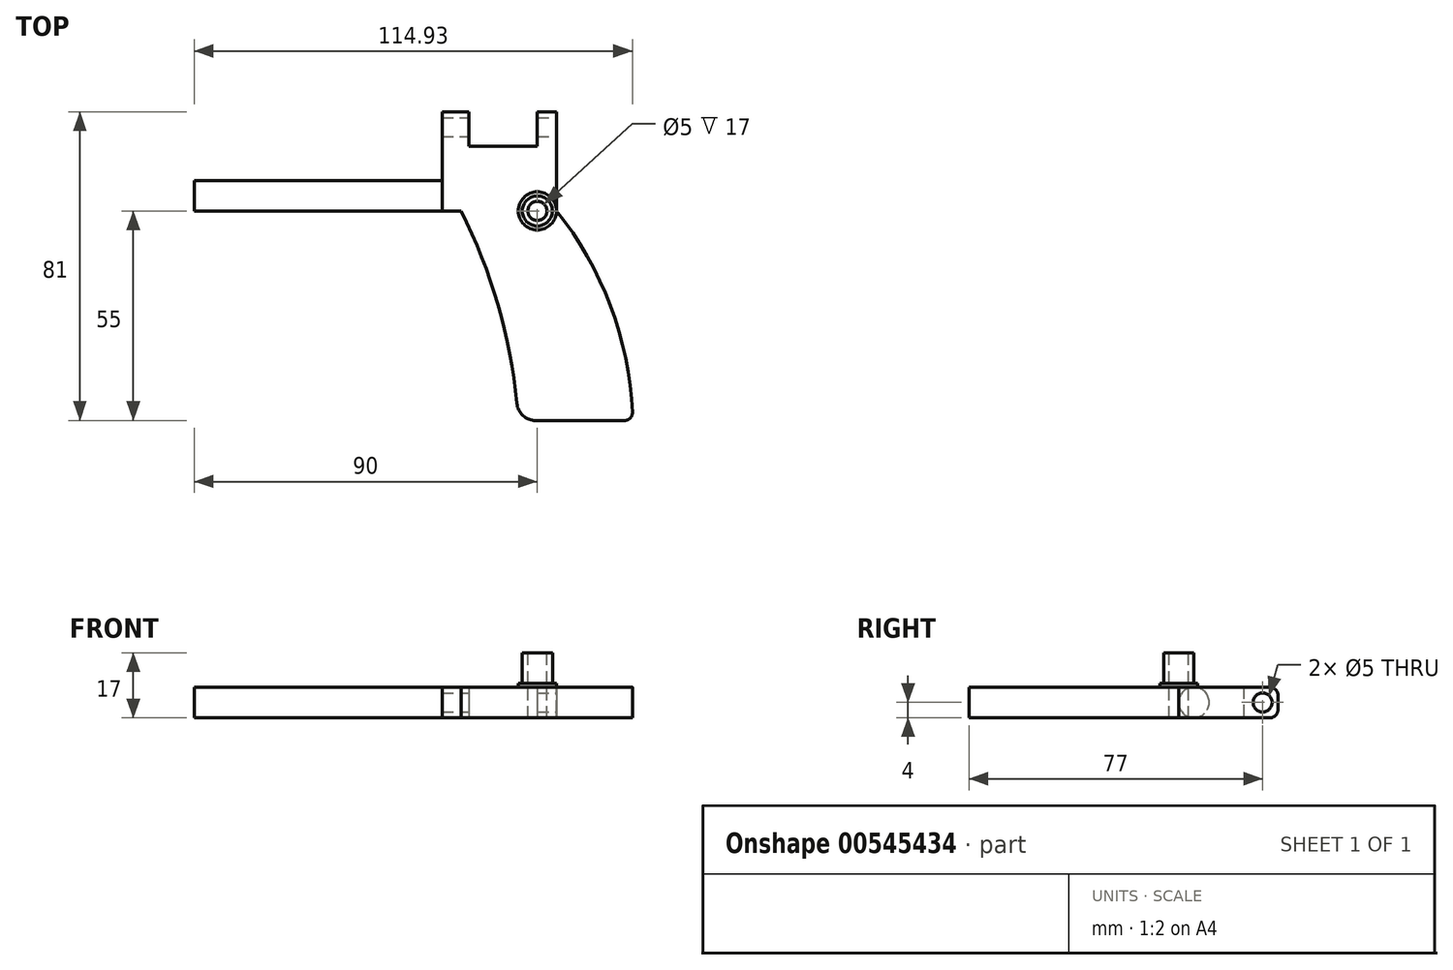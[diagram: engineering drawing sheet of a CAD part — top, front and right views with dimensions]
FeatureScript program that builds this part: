
annotation { "Feature Type Name" : "Feature", "Feature Type Description" : "" }
export const myFeature = defineFeature(function(context is Context, id is Id, definition is map)
    precondition{}
    {
        {
            var Q0;
            Q0=qCreatedBy(makeId("Top.planeOp"),FACE);
            var sketch = newSketch(context, id + "F0", { "sketchPlane" : qUnion([Q0])});
            skLineSegment(sketch, "E0", {"start": v(0, 0) * mm, "end": v(-20, 0) * mm});
            skLineSegment(sketch, "E1", {"start": v(-20, 0) * mm, "end": v(-20, 25) * mm});
            skLineSegment(sketch, "E2", {"start": v(-20, 25) * mm, "end": v(10, 25) * mm});
            skLineSegment(sketch, "E3", {"start": v(10, 25) * mm, "end": v(10, -55) * mm});
            skLineSegment(sketch, "E4", {"start": v(10, -55) * mm, "end": v(0, -55) * mm});
            skLineSegment(sketch, "E5", {"start": v(-5, 25) * mm, "end": v(-5, 17) * mm});
            skLineSegment(sketch, "E6", {"start": v(-5, 17) * mm, "end": v(5, 17) * mm});
            skLineSegment(sketch, "E7", {"start": v(5, 17) * mm, "end": v(5, 25) * mm});
            skLineSegment(sketch, "E8", {"start": v(-5, 17) * mm, "end": v(-13, 17) * mm});
            skLineSegment(sketch, "E9", {"start": v(-13, 17) * mm, "end": v(-13, 25) * mm});
            skLineSegment(sketch, "E10", {"start": v(10, -55) * mm, "end": v(30, -55) * mm});
            skLineSegment(sketch, "E11", {"start": v(0, 0) * mm, "end": v(10, 0) * mm});
            skArc(sketch, "E12", {"start": v(30, -55) * mm, "mid": v(24.54, -25.85) * mm, "end": v(10, 0) * mm});
            skLineSegment(sketch, "E13", {"start": v(-20, 0) * mm, "end": v(-15, 0) * mm});
            skArc(sketch, "E14", {"start": v(0, -55) * mm, "mid": v(-4.75, -26.75) * mm, "end": v(-15, 0) * mm});
            skLineSegment(sketch, "E15", {"start": v(10, 0) * mm, "end": v(10, 15) * mm});
            skLineSegment(sketch, "E16", {"start": v(10, 15) * mm, "end": v(35, 15) * mm});
            skLineSegment(sketch, "E17", {"start": v(35, 15) * mm, "end": v(35, 0) * mm});
            skLineSegment(sketch, "E18", {"start": v(35, 0) * mm, "end": v(16.17, -8.68) * mm});
            skSolve(sketch);
        }
        {
            var Q0;
            Q0=makeQuery(id+"F0.imprint","IMPRINT",FACE,{"disambiguationData":[TD([[makeQuery(id+"F0.imprint","IMPRINT",EDGE,{"derivedFrom":sQuery(id+"F0.wireOp",EDGE,"E0")}),-1.0]])]});
            var Q1;
            {var subQ0=sQuery(id+"F0.wireOp",EDGE,"E4");Q1=makeQuery(id+"F0.imprint","IMPRINT",FACE,{"disambiguationData":[TD([[makeQuery(id+"F0.imprint","IMPRINT",EDGE,{"derivedFrom":subQ0}),-1.0]])]});}
            var Q2;
            {var subQ0=sQuery(id+"F0.wireOp",EDGE,"E10");Q2=makeQuery(id+"F0.imprint","IMPRINT",FACE,{"disambiguationData":[TD([[makeQuery(id+"F0.imprint","IMPRINT",EDGE,{"derivedFrom":subQ0}),1.0]])]});}
            extrude(context, id + "F1", {"entities" : qUnion([Q0, Q1, Q2]), "depth" : 8 * mm, "offsetDistance" : 25 * mm});
        }
        {
            var Q0;
            Q0=makeQuery(id+"F1.opExtrude","SWEPT_FACE",FACE,{"disambiguationData":[OSD([sQuery(id+"F0.wireOp",EDGE,"E3")])]});
            var sketch = newSketch(context, id + "F2", { "sketchPlane" : qUnion([Q0])});
            skLineSegment(sketch, "E19", {"start": v(25, 4) * mm, "end": v(22, 4) * mm});
            skCircle(sketch, "E20", {"center": v(22, 4) * mm, "radius": 2.5 * mm});
            skLineSegment(sketch, "E21", {"start": v(25, 4) * mm, "end": v(4, 4) * mm});
            skSolve(sketch);
        }
        {
            var Q0;
            Q0=makeQuery(id+"F2.imprint","IMPRINT",FACE,{"disambiguationData":[TD([[makeQuery(id+"F2.imprint","IMPRINT",EDGE,{"derivedFrom":sQuery(id+"F2.wireOp",EDGE,"E20")}),1.0]])]});
            extrude(context, id + "F3", {"entities" : qUnion([Q0]), "operationType" : NewBodyOperationType.REMOVE, "oppositeDirection" : true, "depth" : 50 * mm, "offsetDistance" : 25 * mm});
        }
        {
            var Q0;
            Q0=makeQuery(id+"F1.opExtrude","CAP_FACE",FACE,{"disambiguationData":[OSD([sQuery(id+"F0.wireOp",EDGE,"E0"),sQuery(id+"F0.wireOp",EDGE,"E1"),sQuery(id+"F0.wireOp",EDGE,"E2"),sQuery(id+"F0.wireOp",EDGE,"E3"),sQuery(id+"F0.wireOp",EDGE,"E4"),sQuery(id+"F0.wireOp",EDGE,"ejiMLEov-iqfv-gBJr-1tSu-TBK2lTawssNj"),sQuery(id+"F0.wireOp",EDGE,"E6"),sQuery(id+"F0.wireOp",EDGE,"E7"),sQuery(id+"F0.wireOp",EDGE,"E8"),sQuery(id+"F0.wireOp",EDGE,"E9")])],"isStart":true});
            var sketch = newSketch(context, id + "F4", { "sketchPlane" : qUnion([Q0])});
            skLineSegment(sketch, "E22", {"start": v(10, 0) * mm, "end": v(5, 0) * mm});
            skCircle(sketch, "E23", {"center": v(5, 0) * mm, "radius": 5 * mm});
            skSolve(sketch);
        }
        {
            var Q0;
            Q0=makeQuery(id+"F4.imprint","IMPRINT",FACE,{"disambiguationData":[TD([[makeQuery(id+"F4.imprint","IMPRINT",EDGE,{"derivedFrom":sQuery(id+"F4.wireOp",EDGE,"E23")}),1.0]])]});
            extrude(context, id + "F5", {"entities" : qUnion([Q0]), "operationType" : NewBodyOperationType.ADD, "oppositeDirection" : true, "depth" : 9 * mm, "offsetDistance" : 25 * mm});
        }
        {
            var Q0;
            Q0=makeQuery(id+"F5.opExtrude","CAP_FACE",FACE,{"disambiguationData":[OSD([sQuery(id+"F4.wireOp",EDGE,"E23")])],"isStart":false});
            var sketch = newSketch(context, id + "F6", { "sketchPlane" : qUnion([Q0])});
            skLineSegment(sketch, "E24", {"start": v(0, 0) * mm, "end": v(10, 0) * mm});
            skCircle(sketch, "E25", {"center": v(5, 0) * mm, "radius": 3.95 * mm});
            skSolve(sketch);
        }
        {
            var Q0;
            {var subQ0=sQuery(id+"F6.wireOp",EDGE,"E25");var subQ1=sQuery(id+"F6.wireOp",EDGE,"E24");var subQ2=makeQuery(id+"F6.imprint","INTERSECT",VERTEX,{"disambiguationData":[OD(0.0)],"derivedFrom":[subQ1,subQ0]});Q0=makeQuery(id+"F6.imprint","IMPRINT",FACE,{"disambiguationData":[TD([[makeQuery(id+"F6.imprint","IMPRINT",EDGE,{"disambiguationData":[TD([[subQ2,-1.0]])],"derivedFrom":subQ1}),-1.0]])]});}
            var Q1;
            {var subQ0=sQuery(id+"F6.wireOp",EDGE,"E25");var subQ1=sQuery(id+"F6.wireOp",EDGE,"E24");var subQ2=makeQuery(id+"F6.imprint","INTERSECT",VERTEX,{"disambiguationData":[OD(0.0)],"derivedFrom":[subQ1,subQ0]});Q1=makeQuery(id+"F6.imprint","IMPRINT",FACE,{"disambiguationData":[TD([[makeQuery(id+"F6.imprint","IMPRINT",EDGE,{"disambiguationData":[TD([[subQ2,-1.0]])],"derivedFrom":subQ1}),1.0]])]});}
            extrude(context, id + "F7", {"entities" : qUnion([Q0, Q1]), "operationType" : NewBodyOperationType.ADD, "depth" : 8 * mm, "offsetDistance" : 25 * mm});
        }
        {
            var Q0;
            Q0=makeQuery(id+"F7.opExtrude","CAP_FACE",FACE,{"disambiguationData":[OSD([sQuery(id+"F6.wireOp",EDGE,"E25")])],"isStart":false});
            var sketch = newSketch(context, id + "F8", { "sketchPlane" : qUnion([Q0])});
            skLineSegment(sketch, "E26", {"start": v(1.05, 0) * mm, "end": v(8.95, 0) * mm});
            skCircle(sketch, "E27", {"center": v(5, 0) * mm, "radius": 2.5 * mm});
            skSolve(sketch);
        }
        {
            var Q0;
            {var subQ0=sQuery(id+"F8.wireOp",EDGE,"E27");var subQ1=sQuery(id+"F8.wireOp",EDGE,"E26");var subQ2=makeQuery(id+"F8.imprint","INTERSECT",VERTEX,{"disambiguationData":[OD(0.0)],"derivedFrom":[subQ1,subQ0]});Q0=makeQuery(id+"F8.imprint","IMPRINT",FACE,{"disambiguationData":[TD([[makeQuery(id+"F8.imprint","IMPRINT",EDGE,{"disambiguationData":[TD([[subQ2,-1.0]])],"derivedFrom":subQ1}),1.0]])]});}
            var Q1;
            {var subQ0=sQuery(id+"F8.wireOp",EDGE,"E27");var subQ1=sQuery(id+"F8.wireOp",EDGE,"E26");var subQ2=makeQuery(id+"F8.imprint","INTERSECT",VERTEX,{"disambiguationData":[OD(0.0)],"derivedFrom":[subQ1,subQ0]});Q1=makeQuery(id+"F8.imprint","IMPRINT",FACE,{"disambiguationData":[TD([[makeQuery(id+"F8.imprint","IMPRINT",EDGE,{"disambiguationData":[TD([[subQ2,-1.0]])],"derivedFrom":subQ1}),-1.0]])]});}
            extrude(context, id + "F9", {"entities" : qUnion([Q0, Q1]), "operationType" : NewBodyOperationType.REMOVE, "oppositeDirection" : true, "depth" : 25 * mm, "offsetDistance" : 25 * mm});
        }
        {
            var Q0;
            Q0=makeQuery(id+"F1.opExtrude","SWEPT_FACE",FACE,{"disambiguationData":[OSD([sQuery(id+"F0.wireOp",EDGE,"E1")])]});
            var sketch = newSketch(context, id + "F10", { "sketchPlane" : qUnion([Q0])});
            skLineSegment(sketch, "E28", {"start": v(0, 4) * mm, "end": v(-4, 4) * mm});
            skCircle(sketch, "E29", {"center": v(-4, 4) * mm, "radius": 4 * mm});
            skSolve(sketch);
        }
        {
            var Q0;
            {var subQ0=sQuery(id+"F10.wireOp",EDGE,"E29");var subQ1=sQuery(id+"F0.wireOp",EDGE,"E1");var subQ3=makeQuery(id+"F10.imprint","INTERSECT",VERTEX,{"derivedFrom":[makeQuery(id+"F1.opExtrude","CAP_EDGE",EDGE,{"disambiguationData":[OSD([subQ1])],"isStart":false}),subQ0]});Q0=makeQuery(id+"F10.imprint","IMPRINT",FACE,{"disambiguationData":[TD([[makeQuery(id+"F10.imprint","IMPRINT",EDGE,{"disambiguationData":[TD([[subQ3,-1.0]])],"derivedFrom":subQ0}),1.0]])]});}
            extrude(context, id + "F11", {"entities" : qUnion([Q0]), "operationType" : NewBodyOperationType.ADD, "depth" : 65 * mm, "offsetDistance" : 25 * mm});
        }
        {
            var Q0;
            {var subQ0=sQuery(id+"F0.wireOp",EDGE,"E2");Q0=makeQuery(id+"F1.opExtrude","SWEPT_FACE",FACE,{"disambiguationData":[OSD([subQ0]),TDD([makeQuery(id+"F0.imprint","IMPRINT",EDGE,{"disambiguationData":[TD([[makeQuery(id+"F0.imprint","INTERSECT",VERTEX,{"derivedFrom":[sQuery(id+"F0.wireOp",EDGE,"E1"),subQ0]}),-1.0]])],"derivedFrom":subQ0})])]});}
            var Q1;
            {var subQ0=sQuery(id+"F0.wireOp",EDGE,"E2");Q1=makeQuery(id+"F1.opExtrude","SWEPT_FACE",FACE,{"disambiguationData":[OSD([subQ0]),TDD([makeQuery(id+"F0.imprint","IMPRINT",EDGE,{"disambiguationData":[TD([[makeQuery(id+"F0.imprint","INTERSECT",VERTEX,{"derivedFrom":[subQ0,sQuery(id+"F0.wireOp",EDGE,"E3")]}),1.0]])],"derivedFrom":subQ0})])]});}
            extrude(context, id + "F12", {"entities" : qUnion([Q0, Q1]), "operationType" : NewBodyOperationType.ADD, "depth" : 1 * mm, "offsetDistance" : 25 * mm});
        }
        {
            var Q0;
            Q0=makeQuery(id+"F1.opExtrude","SWEPT_EDGE",EDGE,{"disambiguationData":[OSD([sQuery(id+"F0.wireOp",EDGE,"E4"),sQuery(id+"F0.wireOp",EDGE,"BMCMoOl9-liOu-DK5P-EVy5-edYmzgEy00HL"),sQuery(id+"F0.wireOp",EDGE,"nxy6E6z5-Rb4u-HYUF-E6Rq-NDB361eCuCwB")])]});
            fillet(context, id + "F13", {"entities" : qUnion([Q0]), "radius" : 5 * mm, "tangentPropagation" : true, "allowEdgeOverflow" : false});
        }
        {
            var Q0;
            Q0=makeQuery(id+"F1.opExtrude","SWEPT_EDGE",EDGE,{"disambiguationData":[OSD([sQuery(id+"F0.wireOp",EDGE,"E10"),sQuery(id+"F0.wireOp",EDGE,"E12")])]});
            fillet(context, id + "F14", {"entities" : qUnion([Q0]), "radius" : 2 * mm, "tangentPropagation" : true, "allowEdgeOverflow" : false});
        }
        {
            var Q0;
            {var subQ0=sQuery(id+"F0.wireOp",EDGE,"E2");Q0=makeQuery(id+"F12.opExtrude","CAP_EDGE",EDGE,{"disambiguationData":[OSD([subQ0]),TDD([makeQuery(id+"F1.opExtrude","CAP_EDGE",EDGE,{"disambiguationData":[OSD([subQ0]),TDD([makeQuery(id+"F0.imprint","IMPRINT",EDGE,{"disambiguationData":[TD([[makeQuery(id+"F0.imprint","INTERSECT",VERTEX,{"derivedFrom":[sQuery(id+"F0.wireOp",EDGE,"E1"),subQ0]}),-1.0]])],"derivedFrom":subQ0})])],"isStart":false})])],"isStart":false});}
            var Q1;
            {var subQ0=sQuery(id+"F0.wireOp",EDGE,"E2");Q1=makeQuery(id+"F12.opExtrude","CAP_EDGE",EDGE,{"disambiguationData":[OSD([subQ0]),TDD([makeQuery(id+"F1.opExtrude","CAP_EDGE",EDGE,{"disambiguationData":[OSD([subQ0]),TDD([makeQuery(id+"F0.imprint","IMPRINT",EDGE,{"disambiguationData":[TD([[makeQuery(id+"F0.imprint","INTERSECT",VERTEX,{"derivedFrom":[subQ0,sQuery(id+"F0.wireOp",EDGE,"E3")]}),1.0]])],"derivedFrom":subQ0})])],"isStart":false})])],"isStart":false});}
            var Q2;
            {var subQ0=sQuery(id+"F0.wireOp",EDGE,"E2");Q2=makeQuery(id+"F12.opExtrude","CAP_EDGE",EDGE,{"disambiguationData":[OSD([subQ0]),TDD([makeQuery(id+"F1.opExtrude","CAP_EDGE",EDGE,{"disambiguationData":[OSD([subQ0]),TDD([makeQuery(id+"F0.imprint","IMPRINT",EDGE,{"disambiguationData":[TD([[makeQuery(id+"F0.imprint","INTERSECT",VERTEX,{"derivedFrom":[subQ0,sQuery(id+"F0.wireOp",EDGE,"E3")]}),1.0]])],"derivedFrom":subQ0})])],"isStart":true})])],"isStart":false});}
            var Q3;
            {var subQ0=sQuery(id+"F0.wireOp",EDGE,"E2");Q3=makeQuery(id+"F12.opExtrude","CAP_EDGE",EDGE,{"disambiguationData":[OSD([subQ0]),TDD([makeQuery(id+"F1.opExtrude","CAP_EDGE",EDGE,{"disambiguationData":[OSD([subQ0]),TDD([makeQuery(id+"F0.imprint","IMPRINT",EDGE,{"disambiguationData":[TD([[makeQuery(id+"F0.imprint","INTERSECT",VERTEX,{"derivedFrom":[sQuery(id+"F0.wireOp",EDGE,"E1"),subQ0]}),-1.0]])],"derivedFrom":subQ0})])],"isStart":true})])],"isStart":false});}
            fillet(context, id + "F15", {"entities" : qUnion([Q0, Q1, Q2, Q3]), "radius" : 2 * mm, "tangentPropagation" : true, "allowEdgeOverflow" : false});
        }
    });
